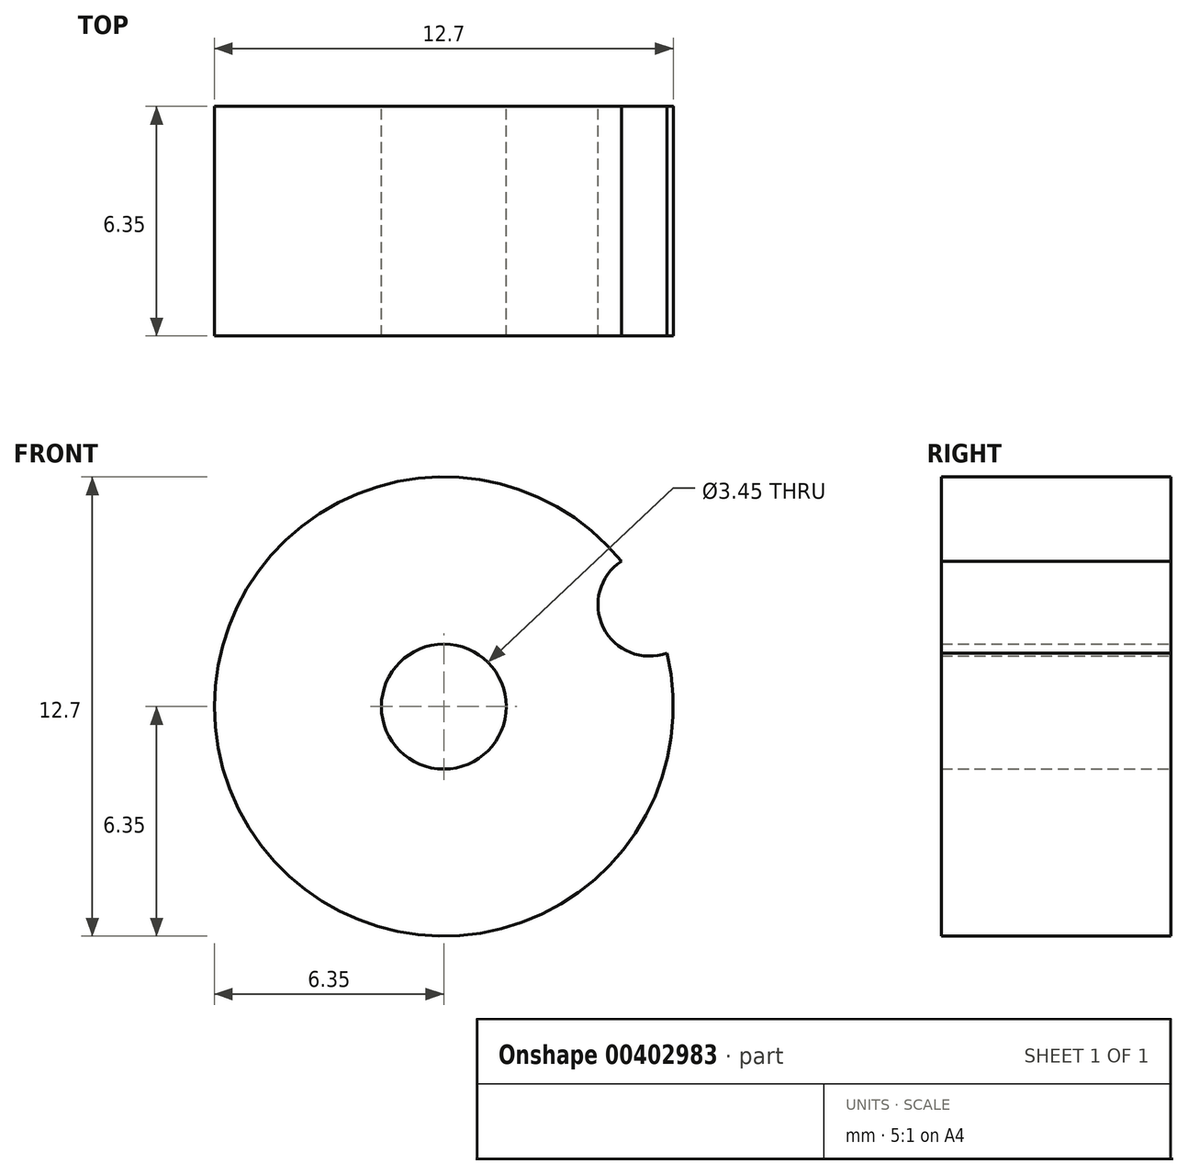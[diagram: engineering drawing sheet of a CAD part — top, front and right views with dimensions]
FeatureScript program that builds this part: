
annotation { "Feature Type Name" : "Feature", "Feature Type Description" : "" }
export const myFeature = defineFeature(function(context is Context, id is Id, definition is map)
    precondition{}
    {
        {
            var Q0;
            Q0=qCreatedBy(makeId("Front.planeOp"),FACE);
            var sketch = newSketch(context, id + "F0", { "sketchPlane" : qUnion([Q0])});
            skCircle(sketch, "E0", {"center": v(0, 0) * mm, "radius": 6.35 * mm});
            skLineSegment(sketch, "E1", {"start": v(-1.51, 6.17) * mm, "end": v(5.82, 7.97) * mm});
            skLineSegment(sketch, "E2", {"start": v(5.82, 7.97) * mm, "end": v(13.2, 6.08) * mm});
            skLineSegment(sketch, "E3", {"start": v(13.2, 6.08) * mm, "end": v(19.28, 6.08) * mm});
            skLineSegment(sketch, "E4", {"start": v(19.28, 6.08) * mm, "end": v(29.28, 14.77) * mm});
            skLineSegment(sketch, "E5", {"start": v(31.9, 11.74) * mm, "end": v(29.28, 14.77) * mm});
            skLineSegment(sketch, "E6", {"start": v(31.9, 11.74) * mm, "end": v(24.35, 5.17) * mm});
            skCircle(sketch, "E7", {"center": v(5.69, 2.82) * mm, "radius": 1.42 * mm});
            skLineSegment(sketch, "E8", {"start": v(24.35, 5.17) * mm, "end": v(13.66, 0) * mm});
            skLineSegment(sketch, "E9", {"start": v(13.66, 0) * mm, "end": v(6.35, 0) * mm});
            skSolve(sketch);
        }
        {
            var Q0;
            {var subQ0=sQuery(id+"F0.wireOp",EDGE,"E0");var subQ1=makeQuery(id+"F0.imprint","INTERSECT",VERTEX,{"derivedFrom":[subQ0,sQuery(id+"F0.wireOp",EDGE,"E9")]});Q0=makeQuery(id+"F0.imprint","IMPRINT",FACE,{"disambiguationData":[TD([[makeQuery(id+"F0.imprint","IMPRINT",EDGE,{"disambiguationData":[TD([[subQ1,-1.0]])],"derivedFrom":subQ0}),1.0]])]});}
            extrude(context, id + "F1", {"entities" : qUnion([Q0]), "depth" : 6.35 * mm});
        }
        {
            var Q0;
            Q0=sQuery(id+"F0.wireOp",VERTEX,"E0.center");
            var Q1;
            Q1=makeQuery(id+"F1.opExtrude","SWEPT_BODY",BODY,{"disambiguationData":[OSD([sQuery(id+"F0.wireOp",EDGE,"E0"),sQuery(id+"F0.wireOp",EDGE,"E7")])]});
            hole(context, id + "F2", {"style" : HoleStyle.SIMPLE, "endStyle" : HoleEndStyle.THROUGH, "oppositeDirection" : true, "standardTappedOrClearance" : lookupTablePath({ "standard" : "ANSI", "fit" : "Normal (ASME)", "engagement" : "75%", "pitch" : "32 tpi", "size" : "#8", "type" : "Tapped" }), "standardBlindInLast" : lookupTablePath({ "fit" : "Free", "standard" : "ANSI", "engagement" : "75%", "pitch" : "32 tpi", "size" : "#8", "type" : "Tapped" }), "holeDiameter" : 3.45 * mm, "showTappedDepth" : true, "isTappedThrough" : true, "tappedDepth" : 12.7 * mm, "tapClearance" : 3, "locations" : qUnion([Q0]), "scope" : qUnion([Q1]), "majorDiameter" : 4.17 * mm});
        }
    });
